# Revit family: Furniture-Workstation-Midmark-IQ_Vitals_Zone-Wall
name_source: partatom
category: Furniture
revit_build: Autodesk Revit 2016 (Build: 20170117_1200(x64)
units: mm (PartAtom-declared; Revit-internal decimal feet)

## family parameters
Cut with Voids When Loaded = No
Host = Face
OmniClass Number = 23.40.70.11.14.11
OmniClass Title = Medical Equipment
Room Calculation Point = No
Shared = No

## types (1)
- Wall Mounted IQ Vitals Zone
    Assembly Code = E1020810
    Default Elevation = 4' - 0"
    Depth = 3' - 0 3/4"
    Description = Wall Mounted IQ Vitals Zone
    Height = 2' - 9 15/16"
    Manufacturer = Midmark
    Material = Paint-Midmark-Mist
    Model = 2-200-0082
    Product Documentation Link = https://my.midmark.com
    Product Name = IQVITALS® ZONE™ WALL MOUNT ARTICULATING ARM
    Product Page URL = http://www.midmark.com
    Type Comments = The expanded range of motion of the IQvitals® Zone™ wall mount articulating arm gives the user the ability to work from the most comfortable position whether seated or standing.
    URL = www.midmark.com
    Width = 1' - 0"

## geometry (parser evidence)
native form markers: Sweep x16
no freeform markers — native parametric forms only
